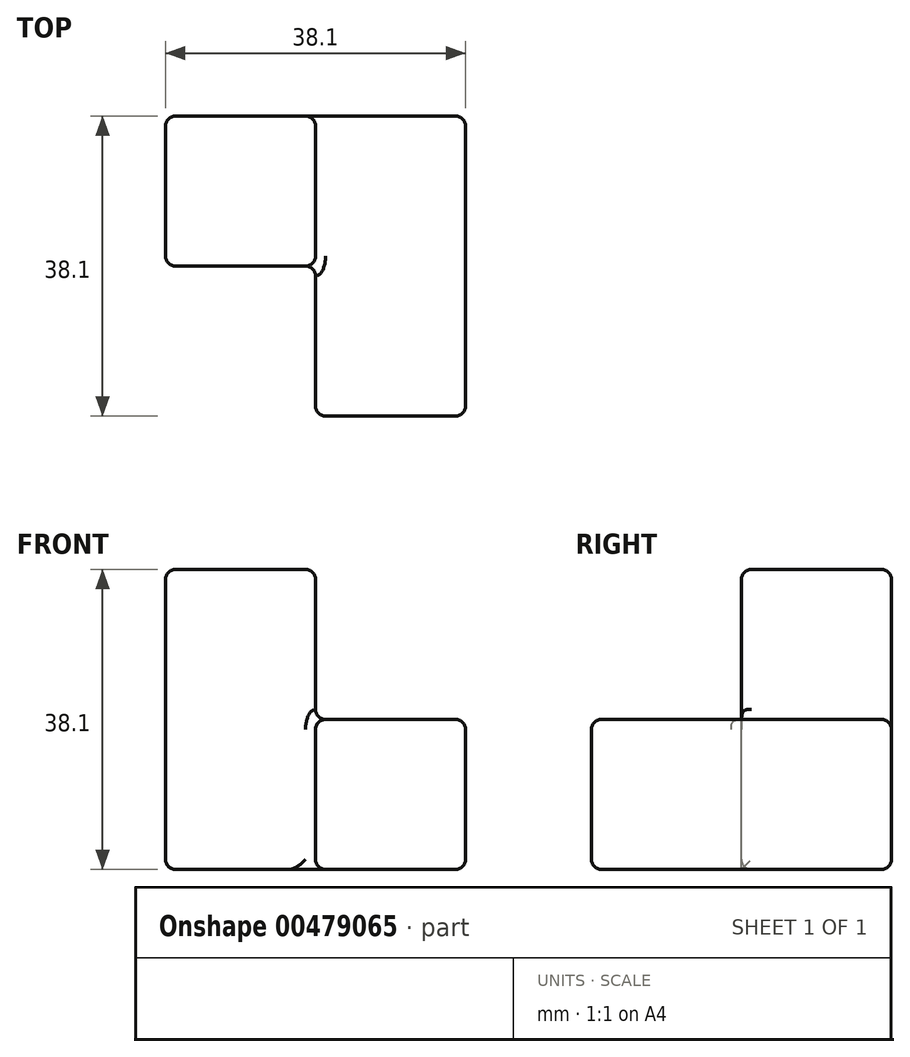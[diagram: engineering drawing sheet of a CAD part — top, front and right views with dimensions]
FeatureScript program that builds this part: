
annotation { "Feature Type Name" : "Feature", "Feature Type Description" : "" }
export const myFeature = defineFeature(function(context is Context, id is Id, definition is map)
    precondition{}
    {
        {
            var Q0;
            Q0=qCreatedBy(makeId("Top.planeOp"),FACE);
            var sketch = newSketch(context, id + "F0", { "sketchPlane" : qUnion([Q0])});
            skLineSegment(sketch, "E0", {"start": v(-19.05, 0) * mm, "end": v(-19.05, 19.05) * mm});
            skLineSegment(sketch, "E1", {"start": v(-19.05, 19.05) * mm, "end": v(19.05, 19.05) * mm});
            skLineSegment(sketch, "E2", {"start": v(19.05, 19.05) * mm, "end": v(19.05, -19.05) * mm});
            skLineSegment(sketch, "E3", {"start": v(19.05, -19.05) * mm, "end": v(0, -19.05) * mm});
            skLineSegment(sketch, "E4", {"start": v(-19.05, 0) * mm, "end": v(0, 0) * mm});
            skLineSegment(sketch, "E5", {"start": v(0, 0) * mm, "end": v(0, -19.05) * mm});
            skSolve(sketch);
        }
        {
            var Q0;
            Q0 = qSketchRegion(id + "F0", true);
            extrude(context, id + "F1", {"entities" : qUnion([Q0]), "oppositeDirection" : true, "depth" : 19.05 * mm});
        }
        {
            var Q0;
            Q0=makeQuery(id+"F1.opExtrude","CAP_FACE",FACE,{"disambiguationData":[OSD([sQuery(id+"F0.wireOp",EDGE,"E0"),sQuery(id+"F0.wireOp",EDGE,"E1"),sQuery(id+"F0.wireOp",EDGE,"E2"),sQuery(id+"F0.wireOp",EDGE,"E3"),sQuery(id+"F0.wireOp",EDGE,"E4"),sQuery(id+"F0.wireOp",EDGE,"E5")])],"isStart":true});
            var sketch = newSketch(context, id + "F2", { "sketchPlane" : qUnion([Q0])});
            skLineSegment(sketch, "E6.bottom", {"start": v(-19.05, 19.05) * mm, "end": v(0, 19.05) * mm});
            skLineSegment(sketch, "E6.top", {"start": v(-19.05, 0) * mm, "end": v(0, 0) * mm});
            skLineSegment(sketch, "E6.left", {"start": v(-19.05, 19.05) * mm, "end": v(-19.05, 0) * mm});
            skLineSegment(sketch, "E6.right", {"start": v(0, 19.05) * mm, "end": v(0, 0) * mm});
            skSolve(sketch);
        }
        {
            var Q0;
            Q0 = qSketchRegion(id + "F2", true);
            extrude(context, id + "F3", {"entities" : qUnion([Q0]), "operationType" : NewBodyOperationType.ADD, "depth" : 19.05 * mm});
        }
        {
            var Q0;
            Q0=makeQuery(id+"F3.opExtrude","CAP_FACE",FACE,{"disambiguationData":[OSD([sQuery(id+"F2.wireOp",EDGE,"E6.bottom"),sQuery(id+"F2.wireOp",EDGE,"E6.top"),sQuery(id+"F2.wireOp",EDGE,"E6.left"),sQuery(id+"F2.wireOp",EDGE,"E6.right")])],"isStart":false});
            var Q1;
            Q1=makeQuery(id+"F3.opExtrude","SWEPT_FACE",FACE,{"disambiguationData":[OSD([sQuery(id+"F2.wireOp",EDGE,"E6.right")])]});
            var Q2;
            Q2=makeQuery(id+"F1.opExtrude","CAP_FACE",FACE,{"disambiguationData":[OSD([sQuery(id+"F0.wireOp",EDGE,"E0"),sQuery(id+"F0.wireOp",EDGE,"E1"),sQuery(id+"F0.wireOp",EDGE,"E2"),sQuery(id+"F0.wireOp",EDGE,"E3"),sQuery(id+"F0.wireOp",EDGE,"E4"),sQuery(id+"F0.wireOp",EDGE,"E5")])],"isStart":true});
            var Q3;
            Q3=makeQuery(id+"F1.opExtrude","SWEPT_FACE",FACE,{"disambiguationData":[OSD([sQuery(id+"F0.wireOp",EDGE,"E2")])]});
            var Q4;
            Q4=makeQuery(id+"F1.opExtrude","SWEPT_FACE",FACE,{"disambiguationData":[OSD([sQuery(id+"F0.wireOp",EDGE,"E3")])]});
            var Q5;
            Q5=makeQuery(id+"F3.boolean.opBoolean","MERGE",FACE,{"derivedFrom":[makeQuery(id+"F1.opExtrude","SWEPT_FACE",FACE,{"disambiguationData":[OSD([sQuery(id+"F0.wireOp",EDGE,"E1")])]}),makeQuery(id+"F3.opExtrude","SWEPT_FACE",FACE,{"disambiguationData":[OSD([sQuery(id+"F2.wireOp",EDGE,"E6.bottom")])]})]});
            var Q6;
            Q6=makeQuery(id+"F3.boolean.opBoolean","MERGE",FACE,{"derivedFrom":[makeQuery(id+"F1.opExtrude","SWEPT_FACE",FACE,{"disambiguationData":[OSD([sQuery(id+"F0.wireOp",EDGE,"E0")])]}),makeQuery(id+"F3.opExtrude","SWEPT_FACE",FACE,{"disambiguationData":[OSD([sQuery(id+"F2.wireOp",EDGE,"E6.left")])]})]});
            var Q7;
            Q7=makeQuery(id+"F1.opExtrude","SWEPT_FACE",FACE,{"disambiguationData":[OSD([sQuery(id+"F0.wireOp",EDGE,"E5")])]});
            fillet(context, id + "F4", {"entities" : qUnion([Q0, Q1, Q2, Q3, Q4, Q5, Q6, Q7]), "radius" : 1.27 * mm, "tangentPropagation" : true, "allowEdgeOverflow" : false});
        }
    });
